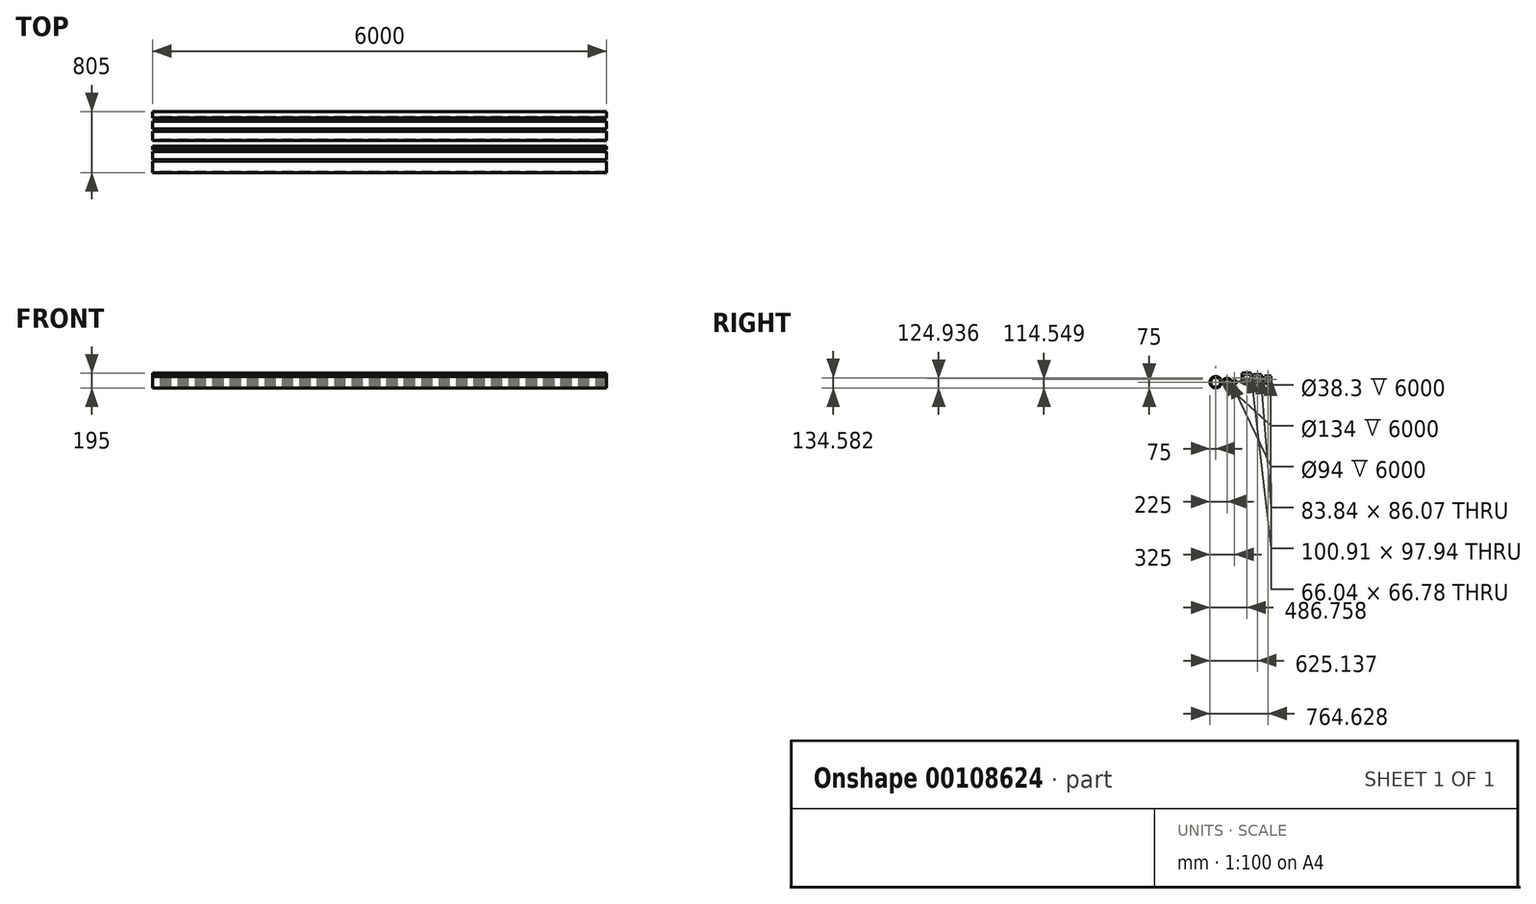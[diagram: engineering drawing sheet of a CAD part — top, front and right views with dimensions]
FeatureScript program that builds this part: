
annotation { "Feature Type Name" : "Feature", "Feature Type Description" : "" }
export const myFeature = defineFeature(function(context is Context, id is Id, definition is map)
    precondition{}
    {
        {
            var Q0;
            Q0=qCreatedBy(makeId("Right.planeOp"),FACE);
            var sketch = newSketch(context, id + "F0", { "sketchPlane" : qUnion([Q0])});
            skLineSegment(sketch, "E0.bottom", {"start": v(0, 0) * mm, "end": v(120, 0) * mm});
            skLineSegment(sketch, "E0.top", {"start": v(0, 120) * mm, "end": v(120, 120) * mm});
            skLineSegment(sketch, "E0.left", {"start": v(0, 0) * mm, "end": v(0, 120) * mm});
            skLineSegment(sketch, "E0.right", {"start": v(120, 0) * mm, "end": v(120, 120) * mm});
            skLineSegment(sketch, "E1.bottom", {"start": v(150, 0) * mm, "end": v(250, 0) * mm});
            skLineSegment(sketch, "E1.top", {"start": v(150, 100) * mm, "end": v(250, 100) * mm});
            skLineSegment(sketch, "E1.left", {"start": v(150, 0) * mm, "end": v(150, 100) * mm});
            skLineSegment(sketch, "E1.right", {"start": v(250, 0) * mm, "end": v(250, 100) * mm});
            skLineSegment(sketch, "E2.bottom", {"start": v(300, 0) * mm, "end": v(380, 0) * mm});
            skLineSegment(sketch, "E2.top", {"start": v(300, 80) * mm, "end": v(380, 80) * mm});
            skLineSegment(sketch, "E2.left", {"start": v(300, 0) * mm, "end": v(300, 80) * mm});
            skLineSegment(sketch, "E2.right", {"start": v(380, 0) * mm, "end": v(380, 80) * mm});
            skCircle(sketch, "E3", {"center": v(-100, 0) * mm, "radius": 24.15 * mm});
            skCircle(sketch, "E4", {"center": v(-200, 0) * mm, "radius": 55 * mm});
            skCircle(sketch, "E5", {"center": v(-200, 0) * mm, "radius": 47 * mm});
            skCircle(sketch, "E6", {"center": v(-100, 0) * mm, "radius": 19.15 * mm});
            skLineSegment(sketch, "E7.bottom", {"start": v(11.3, 10.61) * mm, "end": v(112.21, 10.61) * mm});
            skLineSegment(sketch, "E7.top", {"start": v(11.3, 108.55) * mm, "end": v(112.21, 108.55) * mm});
            skLineSegment(sketch, "E7.left", {"start": v(11.3, 10.61) * mm, "end": v(11.3, 108.55) * mm});
            skLineSegment(sketch, "E7.right", {"start": v(112.21, 10.61) * mm, "end": v(112.21, 108.55) * mm});
            skLineSegment(sketch, "E8.bottom", {"start": v(158.21, 6.9) * mm, "end": v(242.06, 6.9) * mm});
            skLineSegment(sketch, "E8.top", {"start": v(158.21, 92.97) * mm, "end": v(242.06, 92.97) * mm});
            skLineSegment(sketch, "E8.left", {"start": v(158.21, 6.9) * mm, "end": v(158.21, 92.97) * mm});
            skLineSegment(sketch, "E8.right", {"start": v(242.06, 6.9) * mm, "end": v(242.06, 92.97) * mm});
            skLineSegment(sketch, "E9.bottom", {"start": v(306.61, 6.16) * mm, "end": v(372.65, 6.16) * mm});
            skLineSegment(sketch, "E9.top", {"start": v(306.61, 72.94) * mm, "end": v(372.65, 72.94) * mm});
            skLineSegment(sketch, "E9.left", {"start": v(306.61, 6.16) * mm, "end": v(306.61, 72.94) * mm});
            skLineSegment(sketch, "E9.right", {"start": v(372.65, 6.16) * mm, "end": v(372.65, 72.94) * mm});
            skCircle(sketch, "E10", {"center": v(-350, 0) * mm, "radius": 75 * mm});
            skCircle(sketch, "E11", {"center": v(-350, 0) * mm, "radius": 67 * mm});
            skSolve(sketch);
        }
        {
            var Q0;
            Q0=makeQuery(id+"F0.imprint","IMPRINT",FACE,{"disambiguationData":[TD([[makeQuery(id+"F0.imprint","IMPRINT",EDGE,{"derivedFrom":sQuery(id+"F0.wireOp",EDGE,"E4")}),1.0]])]});
            var Q1;
            Q1=makeQuery(id+"F0.imprint","IMPRINT",FACE,{"disambiguationData":[TD([[makeQuery(id+"F0.imprint","IMPRINT",EDGE,{"derivedFrom":sQuery(id+"F0.wireOp",EDGE,"E3")}),1.0]])]});
            var Q2;
            Q2=makeQuery(id+"F0.imprint","IMPRINT",FACE,{"disambiguationData":[TD([[makeQuery(id+"F0.imprint","IMPRINT",EDGE,{"derivedFrom":sQuery(id+"F0.wireOp",EDGE,"E0.bottom")}),1.0]])]});
            var Q3;
            Q3=makeQuery(id+"F0.imprint","IMPRINT",FACE,{"disambiguationData":[TD([[makeQuery(id+"F0.imprint","IMPRINT",EDGE,{"derivedFrom":sQuery(id+"F0.wireOp",EDGE,"E1.bottom")}),1.0]])]});
            var Q4;
            Q4=makeQuery(id+"F0.imprint","IMPRINT",FACE,{"disambiguationData":[TD([[makeQuery(id+"F0.imprint","IMPRINT",EDGE,{"derivedFrom":sQuery(id+"F0.wireOp",EDGE,"E2.bottom")}),1.0]])]});
            var Q5;
            Q5=makeQuery(id+"F0.imprint","IMPRINT",FACE,{"disambiguationData":[TD([[makeQuery(id+"F0.imprint","IMPRINT",EDGE,{"derivedFrom":sQuery(id+"F0.wireOp",EDGE,"E10")}),1.0]])]});
            extrude(context, id + "F1", {"entities" : qUnion([Q0, Q1, Q2, Q3, Q4, Q5]), "depth" : 6000 * mm});
        }
    });
